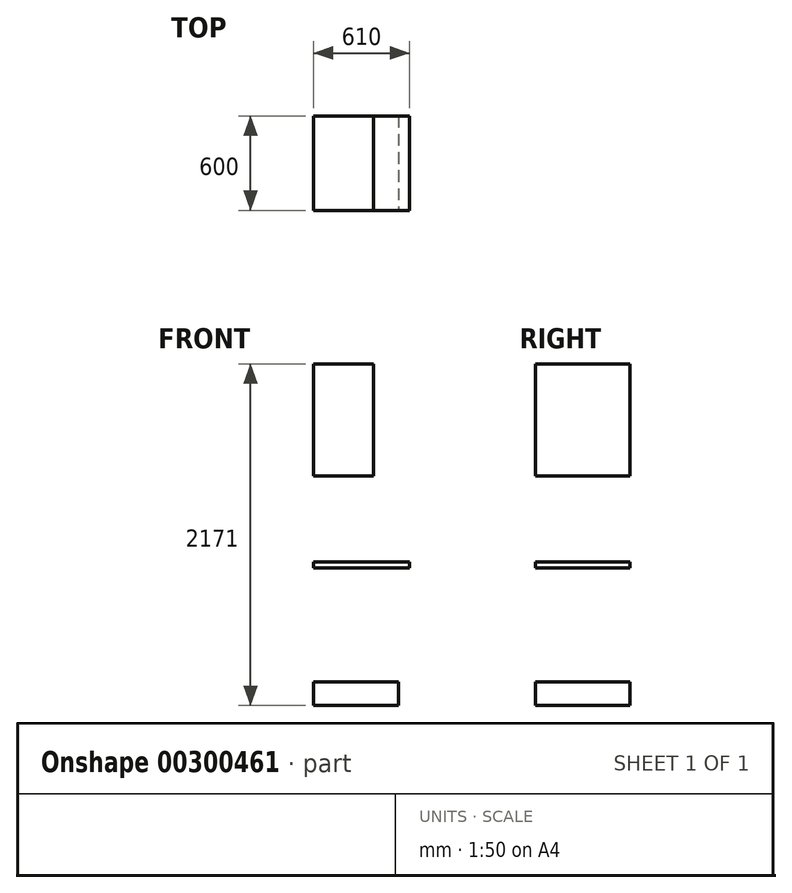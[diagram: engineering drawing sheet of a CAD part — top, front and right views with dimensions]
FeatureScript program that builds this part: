
annotation { "Feature Type Name" : "Feature", "Feature Type Description" : "" }
export const myFeature = defineFeature(function(context is Context, id is Id, definition is map)
    precondition{}
    {
        {
            var Q0;
            Q0=qCreatedBy(makeId("Front.planeOp"),FACE);
            var sketch = newSketch(context, id + "F0", { "sketchPlane" : qUnion([Q0])});
            skLineSegment(sketch, "E0", {"start": v(0, 0) * mm, "end": v(610, 0) * mm, "construction": true});
            skLineSegment(sketch, "E1", {"start": v(610, 0) * mm, "end": v(610, 912) * mm, "construction": true});
            skLineSegment(sketch, "E2", {"start": v(610, 912) * mm, "end": v(0, 912) * mm, "construction": true});
            skLineSegment(sketch, "E3", {"start": v(0, 912) * mm, "end": v(0, 0) * mm, "construction": true});
            skLineSegment(sketch, "E4.bottom", {"start": v(0, 912) * mm, "end": v(610, 912) * mm});
            skLineSegment(sketch, "E4.top", {"start": v(0, 873) * mm, "end": v(610, 873) * mm});
            skLineSegment(sketch, "E4.left", {"start": v(0, 912) * mm, "end": v(0, 873) * mm});
            skLineSegment(sketch, "E4.right", {"start": v(610, 912) * mm, "end": v(610, 873) * mm});
            skLineSegment(sketch, "E5.bottom", {"start": v(0, 873) * mm, "end": v(588, 873) * mm});
            skLineSegment(sketch, "E5.top", {"start": v(0, 151) * mm, "end": v(588, 151) * mm});
            skLineSegment(sketch, "E5.left", {"start": v(0, 873) * mm, "end": v(0, 151) * mm});
            skLineSegment(sketch, "E5.right", {"start": v(588, 873) * mm, "end": v(588, 151) * mm});
            skLineSegment(sketch, "E6.bottom", {"start": v(0, 0) * mm, "end": v(540, 0) * mm});
            skLineSegment(sketch, "E6.top", {"start": v(0, 151) * mm, "end": v(540, 151) * mm});
            skLineSegment(sketch, "E6.left", {"start": v(0, 0) * mm, "end": v(0, 151) * mm});
            skLineSegment(sketch, "E6.right", {"start": v(540, 0) * mm, "end": v(540, 151) * mm});
            skLineSegment(sketch, "E7", {"start": v(0, 912) * mm, "end": v(0, 1458) * mm, "construction": true});
            skLineSegment(sketch, "E8", {"start": v(0, 1458) * mm, "end": v(610, 1458) * mm, "construction": true});
            skLineSegment(sketch, "E9", {"start": v(610, 912) * mm, "end": v(610, 1458) * mm, "construction": true});
            skLineSegment(sketch, "E10", {"start": v(0, 1458) * mm, "end": v(0, 2171) * mm, "construction": true});
            skLineSegment(sketch, "E11", {"start": v(0, 2171) * mm, "end": v(380, 2171) * mm, "construction": true});
            skLineSegment(sketch, "E12", {"start": v(380, 2171) * mm, "end": v(380, 1458) * mm, "construction": true});
            skLineSegment(sketch, "E13.bottom", {"start": v(0, 1458) * mm, "end": v(380, 1458) * mm});
            skLineSegment(sketch, "E13.top", {"start": v(0, 2171) * mm, "end": v(380, 2171) * mm});
            skLineSegment(sketch, "E13.left", {"start": v(0, 1458) * mm, "end": v(0, 2171) * mm});
            skLineSegment(sketch, "E13.right", {"start": v(380, 1458) * mm, "end": v(380, 2171) * mm});
            skLineSegment(sketch, "E14", {"start": v(0, 2171) * mm, "end": v(0, 2721) * mm, "construction": true});
            skLineSegment(sketch, "E15", {"start": v(0, 2721) * mm, "end": v(780.34, 2721) * mm, "construction": true});
            skSolve(sketch);
        }
        {
            var Q0;
            Q0=makeQuery(id+"F0.imprint","IMPRINT",FACE,{"disambiguationData":[TD([[makeQuery(id+"F0.imprint","IMPRINT",EDGE,{"derivedFrom":sQuery(id+"F0.wireOp",EDGE,"E5.bottom")}),-1.0]])]});
            var Q1;
            Q1=makeQuery(id+"F0.imprint","IMPRINT",FACE,{"disambiguationData":[TD([[makeQuery(id+"F0.imprint","IMPRINT",EDGE,{"derivedFrom":sQuery(id+"F0.wireOp",EDGE,"E4.bottom")}),-1.0]])]});
            var Q2;
            Q2=makeQuery(id+"F0.imprint","IMPRINT",FACE,{"disambiguationData":[TD([[makeQuery(id+"F0.imprint","IMPRINT",EDGE,{"derivedFrom":sQuery(id+"F0.wireOp",EDGE,"E6.bottom")}),1.0]])]});
            var Q3;
            Q3=makeQuery(id+"F0.imprint","IMPRINT",FACE,{"disambiguationData":[TD([[makeQuery(id+"F0.imprint","IMPRINT",EDGE,{"derivedFrom":sQuery(id+"F0.wireOp",EDGE,"E13.bottom")}),1.0]])]});
            extrude(context, id + "F1", {"entities" : qUnion([Q0, Q1, Q2, Q3]), "oppositeDirection" : true, "depth" : 600 * mm});
        }
    });
